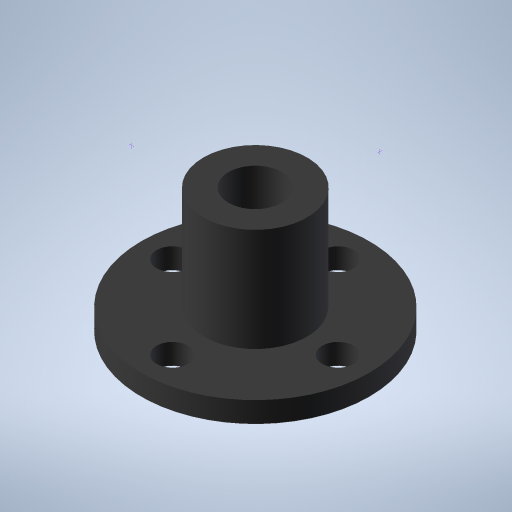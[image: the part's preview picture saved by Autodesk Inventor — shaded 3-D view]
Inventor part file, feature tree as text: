
AUTODESK INVENTOR PART (.ipt)
format: ipt  version: 2024.2 (Build 282272000, 272)  size: 268,288 bytes
history: native  units: mm
features: other x4, sketch x4, extrude x3
ambient origin geometry x8: Origin, YZ Plane, XZ Plane, XY Plane, X Axis, Y Axis, Z Axis, Center Point
bodies: Body1 (feature_tree)
feature tree (11):
  other  "Твердое тело1"
  sketch  "Эскиз1"
  extrude  "Выдавливание1"  Depth=5.2mm
  extrude  "Выдавливание2"  Depth=10.0mm
  sketch  "Эскиз2"
  sketch  "Эскиз3"
  other  "РабОсь4"
  other  "РабОсь5"
  other  "РабПлоскость1"
  extrude  "Выдавливание3"  Depth=22.0mm
  sketch  "Эскиз4"
